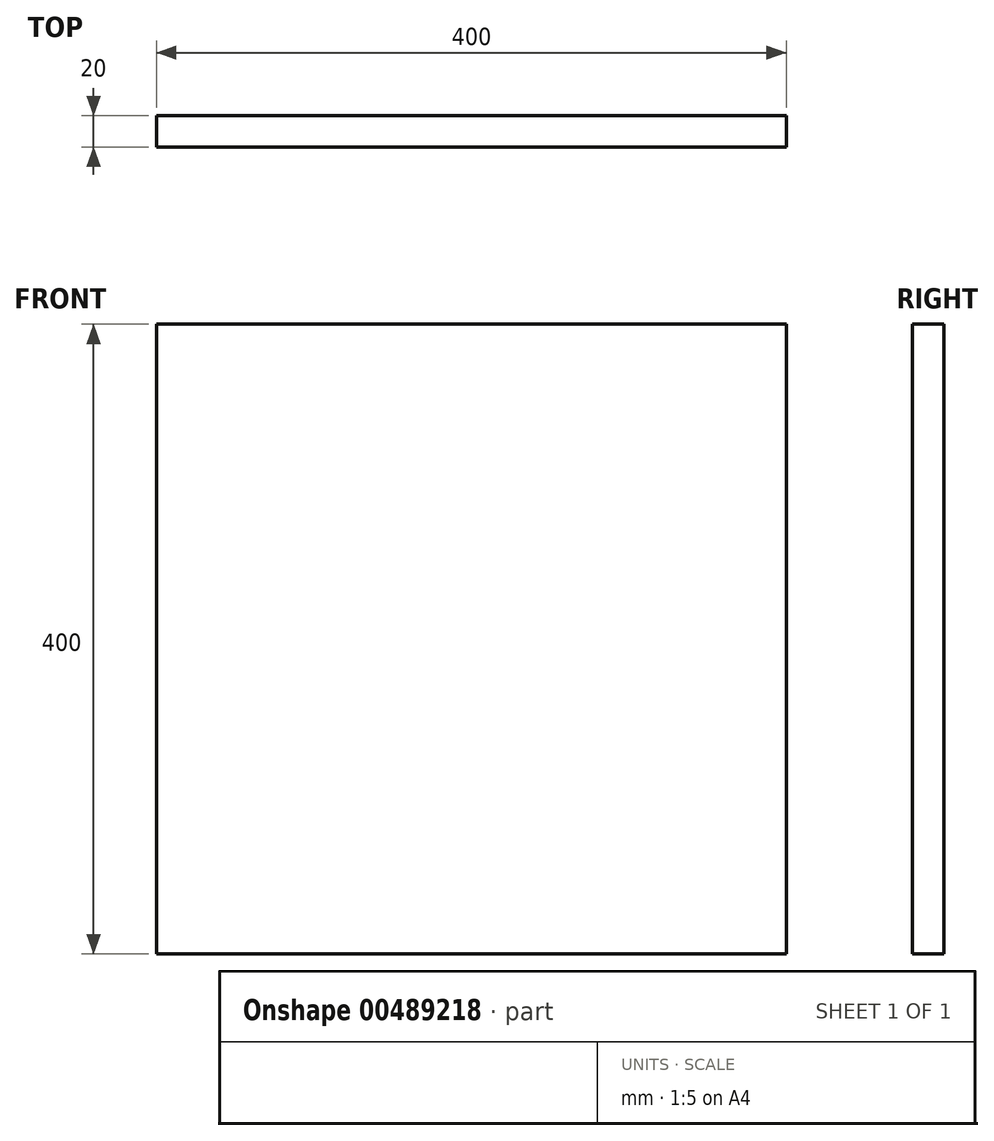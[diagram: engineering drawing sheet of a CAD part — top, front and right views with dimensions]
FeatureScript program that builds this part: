
annotation { "Feature Type Name" : "Feature", "Feature Type Description" : "" }
export const myFeature = defineFeature(function(context is Context, id is Id, definition is map)
    precondition{}
    {
        {
            var Q0;
            Q0=qCreatedBy(makeId("Front.planeOp"),FACE);
            var sketch = newSketch(context, id + "F0", { "sketchPlane" : qUnion([Q0])});
            skLineSegment(sketch, "E0.bottom", {"start": v(0, 0) * mm, "end": v(400, 0) * mm});
            skLineSegment(sketch, "E0.top", {"start": v(0, 400) * mm, "end": v(400, 400) * mm});
            skLineSegment(sketch, "E0.left", {"start": v(0, 0) * mm, "end": v(0, 400) * mm});
            skLineSegment(sketch, "E0.right", {"start": v(400, 0) * mm, "end": v(400, 400) * mm});
            skPoint(sketch, "E1.centerSnap0", {"position": v(400, 200) * mm});
            skPoint(sketch, "E1.centerSnap1", {"position": v(200, 0) * mm});
            skLineSegment(sketch, "E2", {"start": v(200, 200) * mm, "end": v(0, 200) * mm, "construction": true});
            skPoint(sketch, "E3", {"position": v(40, 247) * mm});
            skPoint(sketch, "E4.MirrorP", {"position": v(40, 153) * mm});
            skLineSegment(sketch, "E5", {"start": v(200, 200) * mm, "end": v(200, 282.53) * mm, "construction": true});
            skPoint(sketch, "E5.endSnap0", {"position": v(200, 400) * mm});
            skPoint(sketch, "E6.MirrorP", {"position": v(360, 153) * mm});
            skPoint(sketch, "E7.MirrorP", {"position": v(360, 247) * mm});
            skSolve(sketch);
        }
        {
            var Q0;
            Q0=makeQuery(id+"F0.imprint","IMPRINT",FACE,{"disambiguationData":[TD([[makeQuery(id+"F0.imprint","IMPRINT",EDGE,{"derivedFrom":sQuery(id+"F0.wireOp",EDGE,"E0.bottom")}),1.0]])]});
            extrude(context, id + "F1", {"entities" : qUnion([Q0]), "depth" : 20 * mm, "offsetDistance" : 25 * mm});
        }
    });
